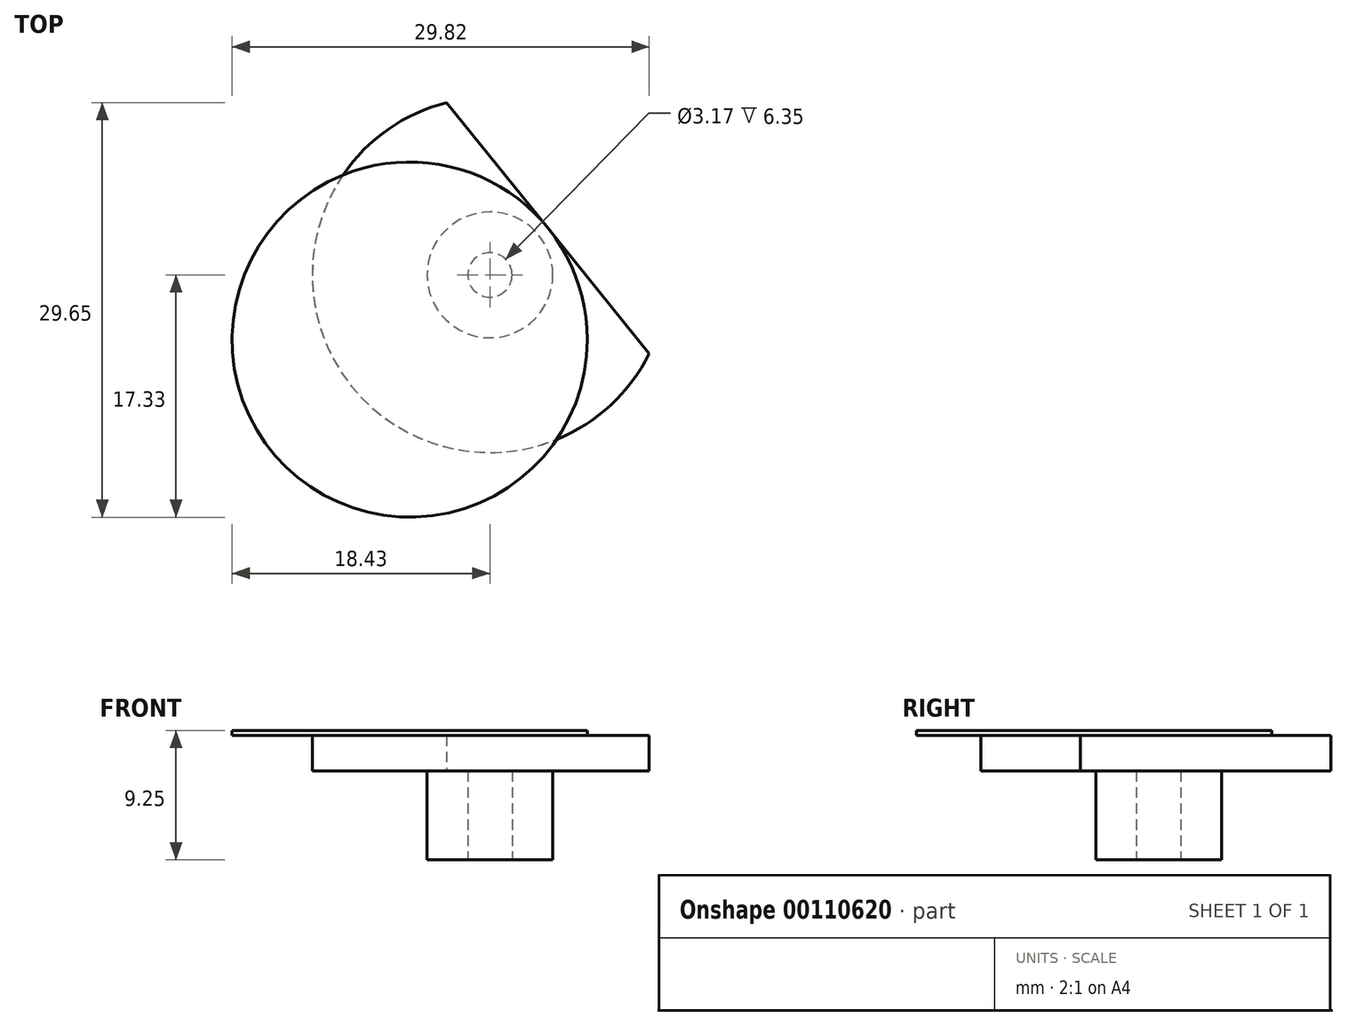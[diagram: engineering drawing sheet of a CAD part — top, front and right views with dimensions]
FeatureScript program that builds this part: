
annotation { "Feature Type Name" : "Feature", "Feature Type Description" : "" }
export const myFeature = defineFeature(function(context is Context, id is Id, definition is map)
    precondition{}
    {
        {
            var Q0;
            Q0=qCreatedBy(makeId("Top.planeOp"),FACE);
            var sketch = newSketch(context, id + "F0", { "sketchPlane" : qUnion([Q0])});
            skCircle(sketch, "E0", {"center": v(0, 0) * mm, "radius": 4.5 * mm});
            skCircle(sketch, "E1", {"center": v(0, 0) * mm, "radius": 1.59 * mm});
            skSolve(sketch);
        }
        {
            var Q0;
            Q0=qSketchRegion(id+"F0",true);
            extrude(context, id + "F1", {"entities" : qUnion([Q0]), "depth" : 6.35 * mm});
        }
        {
            var Q0;
            Q0=makeQuery(id+"F1.opExtrude","CAP_FACE",FACE,{"disambiguationData":[OSD([sQuery(id+"F0.wireOp",EDGE,"E0")])],"isStart":false});
            var sketch = newSketch(context, id + "F2", { "sketchPlane" : qUnion([Q0])});
            skCircle(sketch, "E2", {"center": v(0, 0) * mm, "radius": 12.7 * mm});
            skSolve(sketch);
        }
        {
            var Q0;
            Q0=qSketchRegion(id+"F2",true);
            extrude(context, id + "F3", {"entities" : qUnion([Q0]), "operationType" : NewBodyOperationType.ADD, "depth" : 2.54 * mm});
        }
        {
            var Q0;
            {var subQ0=sQuery(id+"F2.wireOp",EDGE,"E2");Q0=makeQuery(id+"F3.boolean.opBoolean","SPLIT",FACE,{"disambiguationData":[TD([makeQuery(id+"F1.opExtrude","SWEPT_FACE",FACE,{"disambiguationData":[OSD([sQuery(id+"F0.wireOp",EDGE,"E0")])]})])],"derivedFrom":makeQuery(id+"F3.opExtrude","CAP_FACE",FACE,{"disambiguationData":[OSD([subQ0])],"isStart":true})});}
            var sketch = newSketch(context, id + "F4", { "sketchPlane" : qUnion([Q0])});
            skLineSegment(sketch, "E3", {"start": v(19.32, 15.43) * mm, "end": v(-10.04, -20.93) * mm});
            skLineSegment(sketch, "E4", {"start": v(-10.04, -20.93) * mm, "end": v(21.4, -20.93) * mm});
            skLineSegment(sketch, "E5", {"start": v(21.4, -20.93) * mm, "end": v(19.32, 15.43) * mm});
            skSolve(sketch);
        }
        {
            var Q0;
            Q0=qSketchRegion(id+"F4",true);
            extrude(context, id + "F5", {"entities" : qUnion([Q0]), "operationType" : NewBodyOperationType.REMOVE, "endBound" : BoundingType.THROUGH_ALL, "oppositeDirection" : true, "depth" : 25.4 * mm});
        }
        {
            var Q0;
            Q0=makeQuery(id+"F3.opExtrude","CAP_FACE",FACE,{"disambiguationData":[OSD([sQuery(id+"F2.wireOp",EDGE,"E2")])],"isStart":false});
            var sketch = newSketch(context, id + "F6", { "sketchPlane" : qUnion([Q0])});
            skCircle(sketch, "E6", {"center": v(-5.73, -4.63) * mm, "radius": 12.7 * mm});
            skLineSegment(sketch, "E7", {"start": v(0, 0) * mm, "end": v(-40.87, -33) * mm, "construction": true});
            skSolve(sketch);
        }
        {
            var Q0;
            Q0=qSketchRegion(id+"F6",true);
            extrude(context, id + "F7", {"entities" : qUnion([Q0]), "operationType" : NewBodyOperationType.ADD, "depth" : 0.36 * mm});
        }
    });
